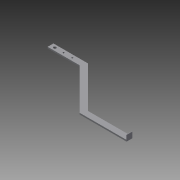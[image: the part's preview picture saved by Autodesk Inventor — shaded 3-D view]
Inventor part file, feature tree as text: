
AUTODESK INVENTOR PART (.ipt)
format: ipt  version: 2013 (Build 170138000, 138)  size: 173,056 bytes
history: native  units: in
note: dims shown in document units (in); Inventor stores cm internally (conversion verified against a paired STEP export)
features: extrude x8, sketch x7
ambient origin geometry x8: Origin, YZ Plane, XZ Plane, XY Plane, X Axis, Y Axis, Z Axis, Center Point
bodies: Solid1 (feature_tree)
feature tree (15):
  extrude  "Extrusion1"  Depth=1.0in
  extrude  "Extrusion2"  Depth=1.0in
  extrude  "Extrusion3"  Depth=9.586in
  extrude  "Extrusion5"  Depth=7.586in
  extrude  "Extrusion7"  Depth=0.25in TaperAngle=0.0deg
  extrude  "Extrusion8"  Depth=1.0in
  extrude  "Extrusion9"  Depth=1.75in TaperAngle=0.0deg
  extrude  "Extrusion10"  Depth=0.25in TaperAngle=0.0deg
  sketch  "Sketch1"  dims[d0=5.25in d1=1.0in]
  sketch  "Sketch3"  dims[d2=112.5deg d3=1.0in]
  sketch  "Sketch5"  dims[d4=135.0deg d5=9.586in]
  sketch  "Sketch7"  dims[d6=0.5in d7=7.586in]
  sketch  "Sketch8"  dims[d8=1.0in d9=0.25in d10=0.0in]
  sketch  "Sketch9"  dims[d13=0.0625in d14=0.0in d15=1.0in]
  sketch  "Sketch10"  dims[d16=1.0in d17=1.75in d18=0.0in d23=0.25in d24=0.0in d31=1.5in d32=180.0deg d33=3.0in d34=0.0in d35=0.25in d36=0.25in d37=1.0in d38=0.0in d39=1.75in d40=1.0in d41=1.5in d42=180.0deg d43=0.25in d44=1.0in d45=0.0in d46=0.25in d47=0.0in d48=0.25in d49=180.0deg d50=0.25in d51=0.0in]
